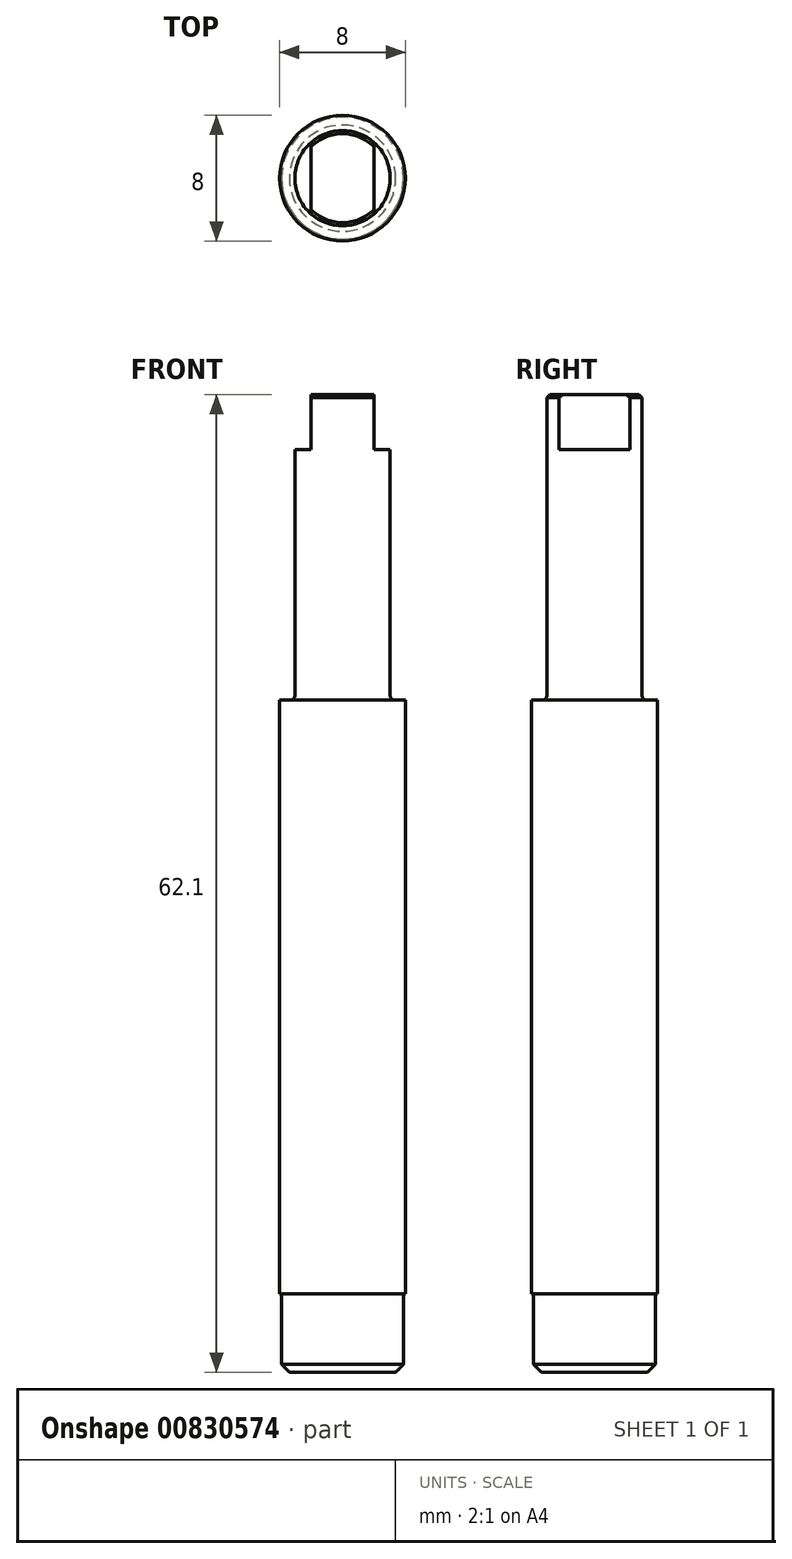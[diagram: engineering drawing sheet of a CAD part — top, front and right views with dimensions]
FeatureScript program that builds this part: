
annotation { "Feature Type Name" : "Feature", "Feature Type Description" : "" }
export const myFeature = defineFeature(function(context is Context, id is Id, definition is map)
    precondition{}
    {
        {
            var Q0;
            Q0=qCreatedBy(makeId("Front.planeOp"),FACE);
            var sketch = newSketch(context, id + "F0", { "sketchPlane" : qUnion([Q0])});
            skLineSegment(sketch, "E0", {"start": v(0, 0) * mm, "end": v(0, 62.1) * mm});
            skLineSegment(sketch, "E1", {"start": v(0, 62.1) * mm, "end": v(3.03, 62.1) * mm});
            skLineSegment(sketch, "E2", {"start": v(3.03, 62.1) * mm, "end": v(3.03, 42.7) * mm});
            skLineSegment(sketch, "E3", {"start": v(3.03, 42.7) * mm, "end": v(4, 42.7) * mm});
            skLineSegment(sketch, "E4", {"start": v(4, 42.7) * mm, "end": v(4, 5) * mm});
            skLineSegment(sketch, "E5", {"start": v(4, 5) * mm, "end": v(3.87, 5) * mm});
            skLineSegment(sketch, "E6", {"start": v(3.87, 5) * mm, "end": v(3.87, 0) * mm});
            skLineSegment(sketch, "E7", {"start": v(3.87, 0) * mm, "end": v(0, 0) * mm});
            skSolve(sketch);
        }
        {
            var Q0;
            Q0=makeQuery(id+"F0.imprint","IMPRINT",FACE,{"disambiguationData":[TD([[makeQuery(id+"F0.imprint","IMPRINT",EDGE,{"derivedFrom":sQuery(id+"F0.wireOp",EDGE,"E0")}),-1.0]])]});
            var Q1;
            Q1=sQuery(id+"F0.wireOp",EDGE,"E0");
            revolve(context, id + "F1", {"surfaceOperationType" : NewSurfaceOperationType.NEW, "entities" : qUnion([Q0]), "axis" : qUnion([Q1]), "revolveType" : RevolveType.FULL});
        }
        {
            var Q0;
            Q0=makeQuery(id+"F1.opRevolve","SWEPT_EDGE",EDGE,{"disambiguationData":[OSD([sQuery(id+"F0.wireOp",EDGE,"E2"),sQuery(id+"F0.wireOp",EDGE,"E3")])]});
            fillet(context, id + "F2", {"entities" : qUnion([Q0]), "radius" : 0.3 * mm, "tangentPropagation" : true, "allowEdgeOverflow" : false});
        }
        {
            var Q0;
            Q0=makeQuery(id+"F1.opRevolve","SWEPT_EDGE",EDGE,{"disambiguationData":[OSD([sQuery(id+"F0.wireOp",EDGE,"E6"),sQuery(id+"F0.wireOp",EDGE,"E7")])]});
            chamfer(context, id + "F3", {"entities" : qUnion([Q0]), "chamferType" : ChamferType.OFFSET_ANGLE, "width" : 0.5 * mm, "oppositeDirection" : false, "angle" : 45 * degree, "tangentPropagation" : true});
        }
        {
            var Q0;
            Q0=makeQuery(id+"F1.opRevolve","SWEPT_FACE",FACE,{"disambiguationData":[OSD([sQuery(id+"F0.wireOp",EDGE,"E1")])]});
            var sketch = newSketch(context, id + "F4", { "sketchPlane" : qUnion([Q0])});
            skLineSegment(sketch, "E8.bottom", {"start": v(-2, 3) * mm, "end": v(-6, 3) * mm});
            skLineSegment(sketch, "E8.top", {"start": v(-2, -3) * mm, "end": v(-6, -3) * mm});
            skLineSegment(sketch, "E8.left", {"start": v(-2, 3) * mm, "end": v(-2, -3) * mm});
            skLineSegment(sketch, "E8.right", {"start": v(-6, 3) * mm, "end": v(-6, -3) * mm});
            skPoint(sketch, "E8.middle", {"position": v(-4, 0) * mm});
            skLineSegment(sketch, "E9.bottom", {"start": v(6, 3) * mm, "end": v(2, 3) * mm});
            skLineSegment(sketch, "E9.top", {"start": v(6, -3) * mm, "end": v(2, -3) * mm});
            skLineSegment(sketch, "E9.left", {"start": v(6, 3) * mm, "end": v(6, -3) * mm});
            skLineSegment(sketch, "E9.right", {"start": v(2, 3) * mm, "end": v(2, -3) * mm});
            skPoint(sketch, "E9.middle", {"position": v(4, 0) * mm});
            skSolve(sketch);
        }
        {
            var Q0;
            Q0 = qSketchRegion(id + "F4", true);
            extrude(context, id + "F5", {"entities" : qUnion([Q0]), "operationType" : NewBodyOperationType.REMOVE, "oppositeDirection" : true, "depth" : (62.1 - 42.7 - 15.9) * mm, "offsetDistance" : 25 * mm});
        }
        {
            var Q0;
            Q0=makeQuery(id+"F5.boolean.opBoolean","COPY",EDGE,{"derivedFrom":makeQuery(id+"F5.opExtrude","CAP_EDGE",EDGE,{"disambiguationData":[OSD([sQuery(id+"F4.wireOp",EDGE,"E9.right")])],"isStart":true})});
            var Q1;
            Q1=makeQuery(id+"F5.boolean.opBoolean","SPLIT",EDGE,{"disambiguationData":[OD(0.0)],"derivedFrom":makeQuery(id+"F1.opRevolve","SWEPT_EDGE",EDGE,{"disambiguationData":[OSD([sQuery(id+"F0.wireOp",EDGE,"E1"),sQuery(id+"F0.wireOp",EDGE,"E2")])]})});
            var Q2;
            Q2=makeQuery(id+"F5.boolean.opBoolean","SPLIT",EDGE,{"disambiguationData":[OD(1.0)],"derivedFrom":makeQuery(id+"F1.opRevolve","SWEPT_EDGE",EDGE,{"disambiguationData":[OSD([sQuery(id+"F0.wireOp",EDGE,"E1"),sQuery(id+"F0.wireOp",EDGE,"E2")])]})});
            var Q3;
            Q3=makeQuery(id+"F5.boolean.opBoolean","COPY",EDGE,{"derivedFrom":makeQuery(id+"F5.opExtrude","CAP_EDGE",EDGE,{"disambiguationData":[OSD([sQuery(id+"F4.wireOp",EDGE,"E8.left")])],"isStart":true})});
            chamfer(context, id + "F6", {"entities" : qUnion([Q0, Q1, Q2, Q3]), "chamferType" : ChamferType.OFFSET_ANGLE, "width" : 0.2 * mm, "oppositeDirection" : false, "angle" : 45 * degree, "tangentPropagation" : true});
        }
    });
